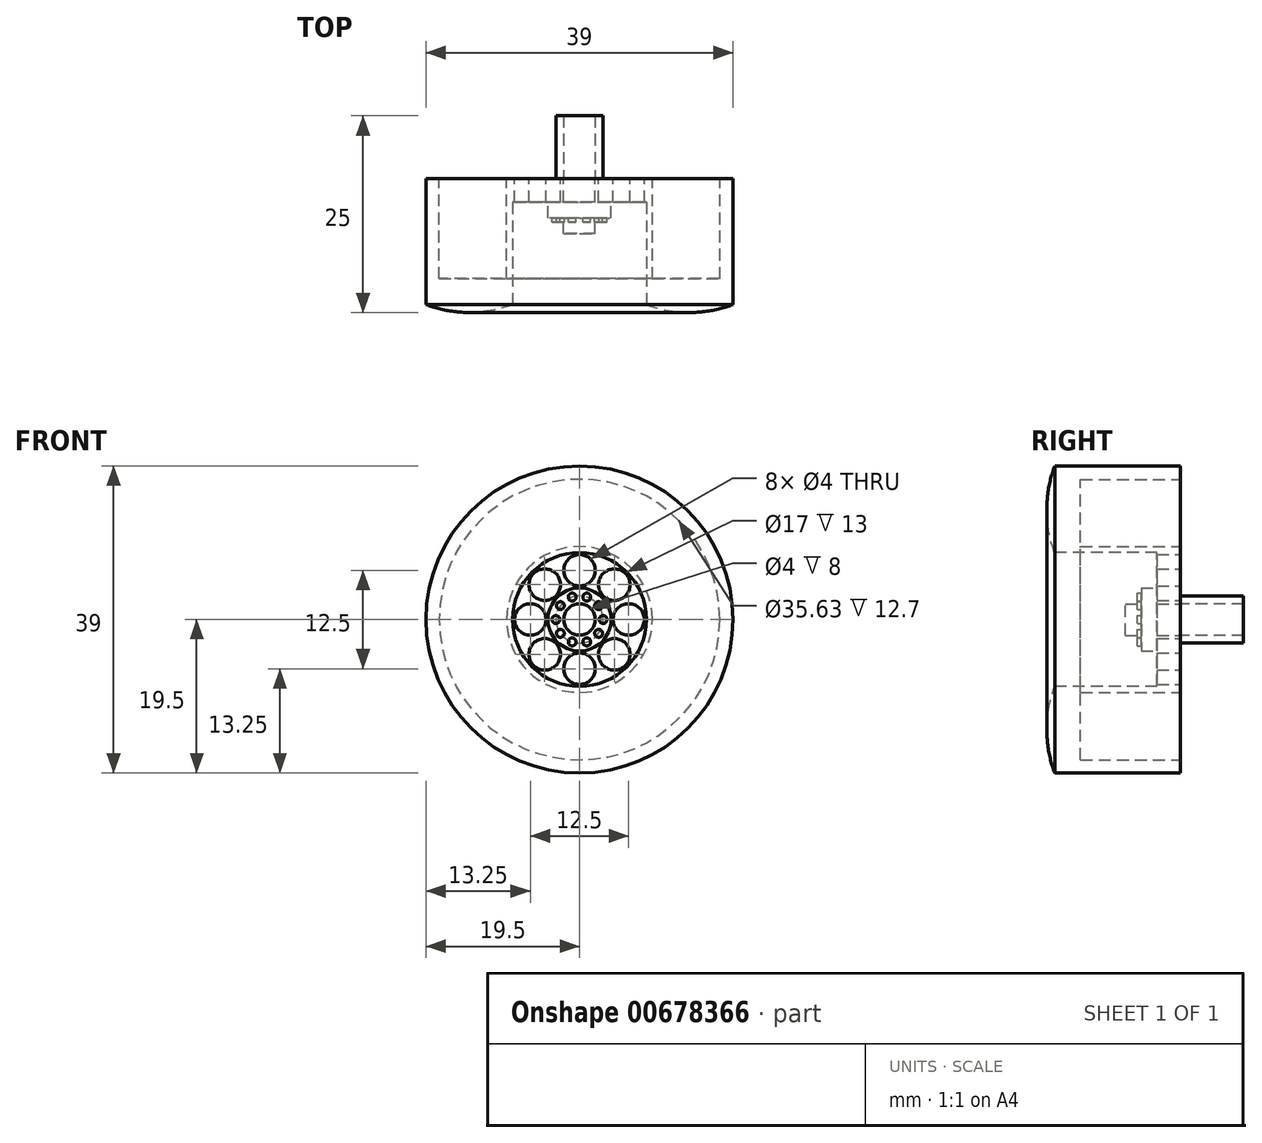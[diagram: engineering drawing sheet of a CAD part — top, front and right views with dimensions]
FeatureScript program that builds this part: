
annotation { "Feature Type Name" : "Feature", "Feature Type Description" : "" }
export const myFeature = defineFeature(function(context is Context, id is Id, definition is map)
    precondition{}
    {
        {
            var Q0;
            Q0=qCreatedBy(makeId("Front.planeOp"),FACE);
            var sketch = newSketch(context, id + "F0", { "sketchPlane" : qUnion([Q0])});
            skCircle(sketch, "E0", {"center": v(0, 0) * mm, "radius": 19.5 * mm});
            skCircle(sketch, "E1", {"center": v(0, 0) * mm, "radius": 18.5 * mm});
            skCircle(sketch, "E2", {"center": v(0, 0) * mm, "radius": 2 * mm});
            skCircle(sketch, "E3", {"center": v(0, 0) * mm, "radius": 4 * mm});
            skPoint(sketch, "E4", {"position": v(4, 0) * mm});
            skPoint(sketch, "E5", {"position": v(3, 0) * mm});
            skCircle(sketch, "E6", {"center": v(3, 0) * mm, "radius": 0.5 * mm});
            skCircle(sketch, "E7.1.0", {"center": v(2.43, 1.76) * mm, "radius": 0.5 * mm});
            skCircle(sketch, "E7.2.0", {"center": v(0.93, 2.85) * mm, "radius": 0.5 * mm});
            skCircle(sketch, "E7.3.0", {"center": v(-0.93, 2.85) * mm, "radius": 0.5 * mm});
            skCircle(sketch, "E7.4.0", {"center": v(-2.43, 1.76) * mm, "radius": 0.5 * mm});
            skCircle(sketch, "E7.5.0", {"center": v(-3, 0) * mm, "radius": 0.5 * mm});
            skCircle(sketch, "E7.6.0", {"center": v(-2.43, -1.76) * mm, "radius": 0.5 * mm});
            skCircle(sketch, "E7.7.0", {"center": v(-0.93, -2.85) * mm, "radius": 0.5 * mm});
            skCircle(sketch, "E7.8.0", {"center": v(0.93, -2.85) * mm, "radius": 0.5 * mm});
            skCircle(sketch, "E7.9.0", {"center": v(2.43, -1.76) * mm, "radius": 0.5 * mm});
            skPoint(sketch, "E8", {"position": v(0, 4) * mm});
            skCircle(sketch, "E9", {"center": v(0, 0) * mm, "radius": 8.5 * mm});
            skPoint(sketch, "E10", {"position": v(0, 8.5) * mm});
            skPoint(sketch, "E11", {"position": v(0, 6.25) * mm});
            skCircle(sketch, "E12", {"center": v(0, 6.25) * mm, "radius": 2 * mm});
            skCircle(sketch, "E13.1.0", {"center": v(-4.42, 4.42) * mm, "radius": 2 * mm});
            skCircle(sketch, "E13.2.0", {"center": v(-6.25, 0) * mm, "radius": 2 * mm});
            skCircle(sketch, "E13.3.0", {"center": v(-4.42, -4.42) * mm, "radius": 2 * mm});
            skCircle(sketch, "E13.4.0", {"center": v(0, -6.25) * mm, "radius": 2 * mm});
            skCircle(sketch, "E13.5.0", {"center": v(4.42, -4.42) * mm, "radius": 2 * mm});
            skCircle(sketch, "E13.6.0", {"center": v(6.25, 0) * mm, "radius": 2 * mm});
            skCircle(sketch, "E13.7.0", {"center": v(4.42, 4.42) * mm, "radius": 2 * mm});
            skPoint(sketch, "E14", {"position": v(0, -19.5) * mm});
            skSolve(sketch);
        }
        {
            var Q0;
            Q0=qCreatedBy(makeId("Right.planeOp"),FACE);
            var sketch = newSketch(context, id + "F1", { "sketchPlane" : qUnion([Q0])});
            skLineSegment(sketch, "E15", {"start": v(0, 0) * mm, "end": v(0, 19.5) * mm});
            skLineSegment(sketch, "E16", {"start": v(0, 19.5) * mm, "end": v(-16, 19.5) * mm});
            skPoint(sketch, "E17", {"position": v(-17, 19.5) * mm});
            skPoint(sketch, "E18", {"position": v(-17, 14) * mm});
            skPoint(sketch, "E19", {"position": v(-16, 8.5) * mm});
            skArc(sketch, "E20", {"start": v(-16, 19.5) * mm, "mid": v(-17, 14) * mm, "end": v(-16, 8.5) * mm});
            skLineSegment(sketch, "E21", {"start": v(-16, 8.5) * mm, "end": v(-3, 8.5) * mm});
            skPoint(sketch, "E22", {"position": v(-3, 8.5) * mm});
            skLineSegment(sketch, "E23", {"start": v(-3, 8.5) * mm, "end": v(-3, 0) * mm});
            skLineSegment(sketch, "E24", {"start": v(-3, 0) * mm, "end": v(0, 0) * mm});
            skPoint(sketch, "E25.orphan", {"position": v(0, 8.5) * mm});
            skSolve(sketch);
        }
        {
            var Q0;
            Q0=makeQuery(id+"F1.imprint","IMPRINT",FACE,{"disambiguationData":[TD([[makeQuery(id+"F1.imprint","IMPRINT",EDGE,{"derivedFrom":sQuery(id+"F1.wireOp",EDGE,"E15")}),1.0]])]});
            var Q1;
            Q1=sQuery(id+"F1.wireOp",EDGE,"E24");
            revolve(context, id + "F2", {"surfaceOperationType" : NewSurfaceOperationType.NEW, "entities" : qUnion([Q0]), "axis" : qUnion([Q1]), "revolveType" : RevolveType.FULL});
        }
        {
            var Q0;
            Q0=makeQuery(id+"F0.imprint","IMPRINT",FACE,{"disambiguationData":[TD([[makeQuery(id+"F0.imprint","IMPRINT",EDGE,{"derivedFrom":sQuery(id+"F0.wireOp",EDGE,"E12")}),1.0]])]});
            var Q1;
            Q1=makeQuery(id+"F0.imprint","IMPRINT",FACE,{"disambiguationData":[TD([[makeQuery(id+"F0.imprint","IMPRINT",EDGE,{"derivedFrom":sQuery(id+"F0.wireOp",EDGE,"E13.1.0")}),1.0]])]});
            var Q2;
            Q2=makeQuery(id+"F0.imprint","IMPRINT",FACE,{"disambiguationData":[TD([[makeQuery(id+"F0.imprint","IMPRINT",EDGE,{"derivedFrom":sQuery(id+"F0.wireOp",EDGE,"E13.2.0")}),1.0]])]});
            var Q3;
            Q3=makeQuery(id+"F0.imprint","IMPRINT",FACE,{"disambiguationData":[TD([[makeQuery(id+"F0.imprint","IMPRINT",EDGE,{"derivedFrom":sQuery(id+"F0.wireOp",EDGE,"E13.3.0")}),1.0]])]});
            var Q4;
            Q4=makeQuery(id+"F0.imprint","IMPRINT",FACE,{"disambiguationData":[TD([[makeQuery(id+"F0.imprint","IMPRINT",EDGE,{"derivedFrom":sQuery(id+"F0.wireOp",EDGE,"E13.4.0")}),1.0]])]});
            var Q5;
            Q5=makeQuery(id+"F0.imprint","IMPRINT",FACE,{"disambiguationData":[TD([[makeQuery(id+"F0.imprint","IMPRINT",EDGE,{"derivedFrom":sQuery(id+"F0.wireOp",EDGE,"E13.5.0")}),1.0]])]});
            var Q6;
            Q6=makeQuery(id+"F0.imprint","IMPRINT",FACE,{"disambiguationData":[TD([[makeQuery(id+"F0.imprint","IMPRINT",EDGE,{"derivedFrom":sQuery(id+"F0.wireOp",EDGE,"E13.6.0")}),1.0]])]});
            var Q7;
            Q7=makeQuery(id+"F0.imprint","IMPRINT",FACE,{"disambiguationData":[TD([[makeQuery(id+"F0.imprint","IMPRINT",EDGE,{"derivedFrom":sQuery(id+"F0.wireOp",EDGE,"E13.7.0")}),1.0]])]});
            extrude(context, id + "F3", {"entities" : qUnion([Q0, Q1, Q2, Q3, Q4, Q5, Q6, Q7]), "operationType" : NewBodyOperationType.REMOVE, "depth" : 32 * mm, "offsetDistance" : 25.4 * mm});
        }
        {
            var Q0;
            Q0=makeQuery(id+"F0.imprint","IMPRINT",FACE,{"disambiguationData":[TD([[makeQuery(id+"F0.imprint","IMPRINT",EDGE,{"derivedFrom":sQuery(id+"F0.wireOp",EDGE,"E2")}),-1.0]])]});
            extrude(context, id + "F4", {"entities" : qUnion([Q0]), "operationType" : NewBodyOperationType.ADD, "depth" : 5 * mm, "offsetDistance" : 25.4 * mm});
        }
        {
            var Q0;
            Q0=makeQuery(id+"F0.imprint","IMPRINT",FACE,{"disambiguationData":[TD([[makeQuery(id+"F0.imprint","IMPRINT",EDGE,{"derivedFrom":sQuery(id+"F0.wireOp",EDGE,"E7.2.0")}),1.0]])]});
            var Q1;
            Q1=makeQuery(id+"F0.imprint","IMPRINT",FACE,{"disambiguationData":[TD([[makeQuery(id+"F0.imprint","IMPRINT",EDGE,{"derivedFrom":sQuery(id+"F0.wireOp",EDGE,"E7.3.0")}),1.0]])]});
            var Q2;
            Q2=makeQuery(id+"F0.imprint","IMPRINT",FACE,{"disambiguationData":[TD([[makeQuery(id+"F0.imprint","IMPRINT",EDGE,{"derivedFrom":sQuery(id+"F0.wireOp",EDGE,"E7.4.0")}),1.0]])]});
            var Q3;
            Q3=makeQuery(id+"F0.imprint","IMPRINT",FACE,{"disambiguationData":[TD([[makeQuery(id+"F0.imprint","IMPRINT",EDGE,{"derivedFrom":sQuery(id+"F0.wireOp",EDGE,"E7.5.0")}),1.0]])]});
            var Q4;
            Q4=makeQuery(id+"F0.imprint","IMPRINT",FACE,{"disambiguationData":[TD([[makeQuery(id+"F0.imprint","IMPRINT",EDGE,{"derivedFrom":sQuery(id+"F0.wireOp",EDGE,"E7.6.0")}),1.0]])]});
            var Q5;
            Q5=makeQuery(id+"F0.imprint","IMPRINT",FACE,{"disambiguationData":[TD([[makeQuery(id+"F0.imprint","IMPRINT",EDGE,{"derivedFrom":sQuery(id+"F0.wireOp",EDGE,"E7.7.0")}),1.0]])]});
            var Q6;
            Q6=makeQuery(id+"F0.imprint","IMPRINT",FACE,{"disambiguationData":[TD([[makeQuery(id+"F0.imprint","IMPRINT",EDGE,{"derivedFrom":sQuery(id+"F0.wireOp",EDGE,"E7.8.0")}),1.0]])]});
            var Q7;
            Q7=makeQuery(id+"F0.imprint","IMPRINT",FACE,{"disambiguationData":[TD([[makeQuery(id+"F0.imprint","IMPRINT",EDGE,{"derivedFrom":sQuery(id+"F0.wireOp",EDGE,"E7.9.0")}),1.0]])]});
            var Q8;
            Q8=makeQuery(id+"F0.imprint","IMPRINT",FACE,{"disambiguationData":[TD([[makeQuery(id+"F0.imprint","IMPRINT",EDGE,{"derivedFrom":sQuery(id+"F0.wireOp",EDGE,"E6")}),1.0]])]});
            var Q9;
            Q9=makeQuery(id+"F0.imprint","IMPRINT",FACE,{"disambiguationData":[TD([[makeQuery(id+"F0.imprint","IMPRINT",EDGE,{"derivedFrom":sQuery(id+"F0.wireOp",EDGE,"E7.1.0")}),1.0]])]});
            extrude(context, id + "F5", {"entities" : qUnion([Q0, Q1, Q2, Q3, Q4, Q5, Q6, Q7, Q8, Q9]), "operationType" : NewBodyOperationType.ADD, "depth" : 5.5 * mm, "offsetDistance" : 25.4 * mm});
        }
        {
            var Q0;
            Q0=makeQuery(id+"F0.imprint","IMPRINT",FACE,{"disambiguationData":[TD([[makeQuery(id+"F0.imprint","IMPRINT",EDGE,{"derivedFrom":sQuery(id+"F0.wireOp",EDGE,"E2")}),1.0]])]});
            extrude(context, id + "F6", {"entities" : qUnion([Q0]), "operationType" : NewBodyOperationType.ADD, "depth" : 7 * mm, "offsetDistance" : 25.4 * mm});
        }
        {
            var Q0;
            Q0=makeQuery(id+"F0.imprint","IMPRINT",FACE,{"disambiguationData":[TD([[makeQuery(id+"F0.imprint","IMPRINT",EDGE,{"derivedFrom":sQuery(id+"F0.wireOp",EDGE,"E1")}),1.0]])]});
            var sketch = newSketch(context, id + "F7", { "sketchPlane" : qUnion([Q0])});
            skCircle(sketch, "E26", {"center": v(0, 0) * mm, "radius": 17.82 * mm});
            skCircle(sketch, "E27", {"center": v(0, 0) * mm, "radius": 9.26 * mm});
            skCircle(sketch, "E28", {"center": v(0, 0) * mm, "radius": 2 * mm});
            skCircle(sketch, "E29", {"center": v(0, 0) * mm, "radius": 3 * mm});
            skSolve(sketch);
        }
        {
            var Q0;
            Q0=makeQuery(id+"F7.imprint","IMPRINT",FACE,{"disambiguationData":[TD([[makeQuery(id+"F7.imprint","IMPRINT",EDGE,{"derivedFrom":sQuery(id+"F7.wireOp",EDGE,"E28")}),-1.0]])]});
            extrude(context, id + "F8", {"entities" : qUnion([Q0]), "operationType" : NewBodyOperationType.ADD, "oppositeDirection" : true, "depth" : 8 * mm, "offsetDistance" : 25.4 * mm});
        }
        {
            var Q0;
            Q0=makeQuery(id+"F7.imprint","IMPRINT",FACE,{"disambiguationData":[TD([[makeQuery(id+"F7.imprint","IMPRINT",EDGE,{"derivedFrom":sQuery(id+"F7.wireOp",EDGE,"E26")}),1.0]])]});
            extrude(context, id + "F9", {"entities" : qUnion([Q0]), "operationType" : NewBodyOperationType.REMOVE, "depth" : 12.7 * mm, "offsetDistance" : 25.4 * mm});
        }
    });
